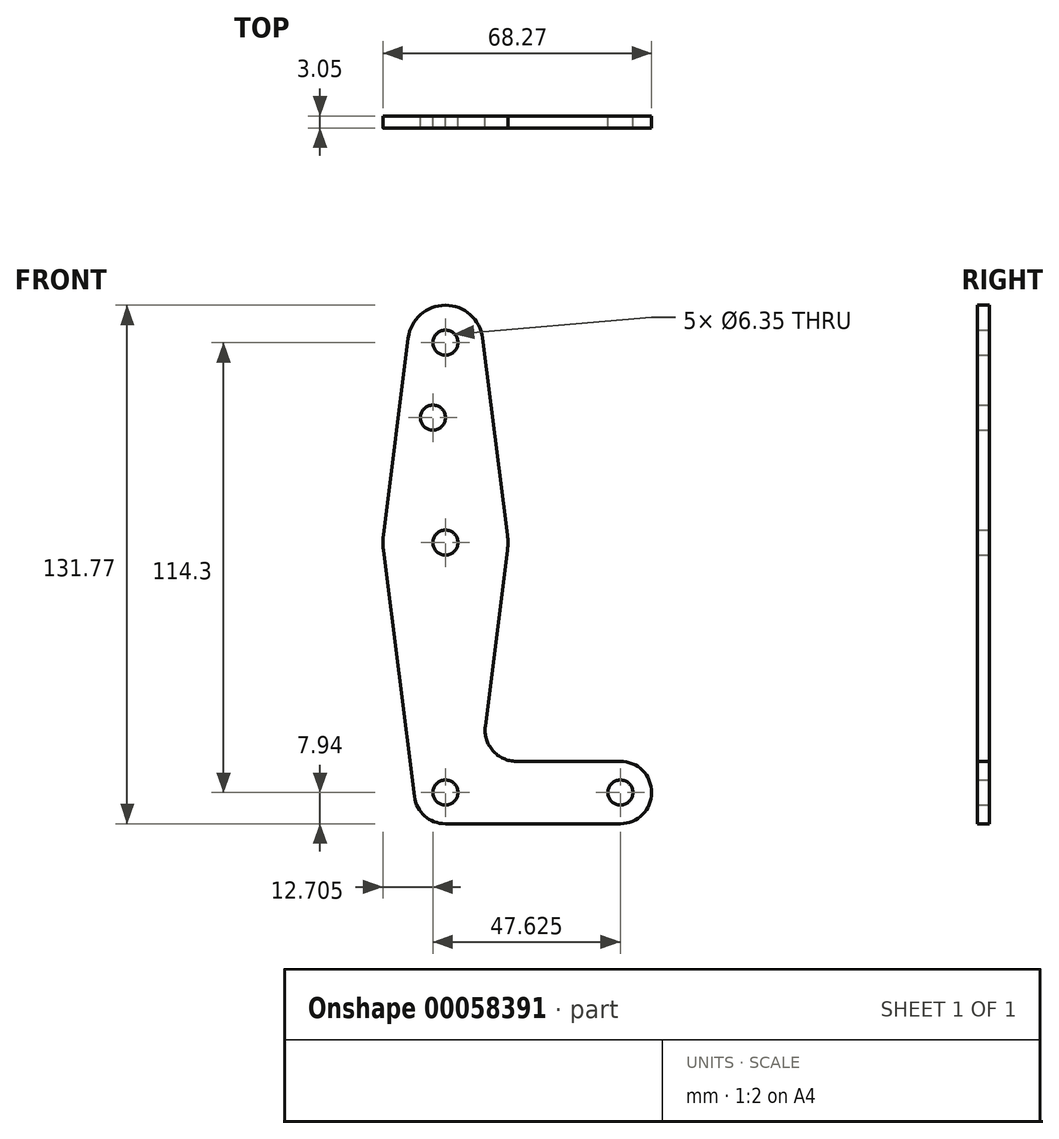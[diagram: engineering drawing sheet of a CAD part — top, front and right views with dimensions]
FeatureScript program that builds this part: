
annotation { "Feature Type Name" : "Feature", "Feature Type Description" : "" }
export const myFeature = defineFeature(function(context is Context, id is Id, definition is map)
    precondition{}
    {
        {
            var Q0;
            Q0=qCreatedBy(makeId("Front.planeOp"),FACE);
            var sketch = newSketch(context, id + "F0", { "sketchPlane" : qUnion([Q0])});
            skCircle(sketch, "E0", {"center": v(0, 0) * mm, "radius": 7.94 * mm});
            skCircle(sketch, "E1", {"center": v(0, 63.5) * mm, "radius": 15.88 * mm});
            skCircle(sketch, "E2", {"center": v(0, 114.3) * mm, "radius": 9.53 * mm});
            skCircle(sketch, "E3", {"center": v(44.45, 0) * mm, "radius": 7.94 * mm});
            skLineSegment(sketch, "E4", {"start": v(-9.45, 115.5) * mm, "end": v(-15.75, 65.48) * mm});
            skLineSegment(sketch, "E5", {"start": v(9.45, 115.5) * mm, "end": v(15.75, 65.48) * mm});
            skLineSegment(sketch, "E6", {"start": v(-15.75, 61.52) * mm, "end": v(-7.88, -1) * mm});
            skLineSegment(sketch, "E7", {"start": v(15.75, 61.52) * mm, "end": v(10.13, 16.88) * mm});
            skLineSegment(sketch, "E8", {"start": v(18.01, 7.94) * mm, "end": v(44.45, 7.94) * mm});
            skLineSegment(sketch, "E9", {"start": v(0, -7.94) * mm, "end": v(44.45, -7.94) * mm});
            skCircle(sketch, "E10", {"center": v(0, 114.3) * mm, "radius": 3.18 * mm});
            skLineSegment(sketch, "E11", {"start": v(0, 0) * mm, "end": v(0, 144.52) * mm, "construction": true});
            skLineSegment(sketch, "E12", {"start": v(0, 0) * mm, "end": v(105.27, 0) * mm, "construction": true});
            skCircle(sketch, "E13", {"center": v(0, 63.5) * mm, "radius": 3.18 * mm});
            skCircle(sketch, "E14", {"center": v(44.45, 0) * mm, "radius": 3.18 * mm});
            skCircle(sketch, "E15", {"center": v(0, 0) * mm, "radius": 3.18 * mm});
            skPoint(sketch, "E16.newPointA", {"position": v(0, 7.94) * mm});
            skArc(sketch, "E16.filletArc", {"start": v(10.13, 16.88) * mm, "mid": v(12.05, 10.63) * mm, "end": v(18.01, 7.94) * mm});
            skCircle(sketch, "E17", {"center": v(-3.18, 95.25) * mm, "radius": 3.18 * mm});
            skPoint(sketch, "E17.first.point", {"position": v(0, 95.25) * mm});
            skPoint(sketch, "E17.second.point", {"position": v(-5.92, 96.84) * mm});
            skPoint(sketch, "E17.third.point", {"position": v(-5.67, 93.29) * mm});
            skSolve(sketch);
        }
        {
            var Q0;
            Q0=makeQuery(id+"F0.imprint","IMPRINT",FACE,{"disambiguationData":[TD([[makeQuery(id+"F0.imprint","IMPRINT",EDGE,{"derivedFrom":sQuery(id+"F0.wireOp",EDGE,"E10")}),-1.0]])]});
            var Q1;
            {var subQ1=sQuery(id+"F0.wireOp",EDGE,"E4");Q1=makeQuery(id+"F0.imprint","IMPRINT",FACE,{"disambiguationData":[TD([[makeQuery(id+"F0.imprint","IMPRINT",EDGE,{"derivedFrom":subQ1}),1.0]])]});}
            var Q2;
            Q2=makeQuery(id+"F0.imprint","IMPRINT",FACE,{"disambiguationData":[TD([[makeQuery(id+"F0.imprint","IMPRINT",EDGE,{"derivedFrom":sQuery(id+"F0.wireOp",EDGE,"E13")}),-1.0]])]});
            var Q3;
            {var subQ0=sQuery(id+"F0.wireOp",EDGE,"E6");Q3=makeQuery(id+"F0.imprint","IMPRINT",FACE,{"disambiguationData":[TD([[makeQuery(id+"F0.imprint","IMPRINT",EDGE,{"derivedFrom":subQ0}),1.0]])]});}
            var Q4;
            Q4=makeQuery(id+"F0.imprint","IMPRINT",FACE,{"disambiguationData":[TD([[makeQuery(id+"F0.imprint","IMPRINT",EDGE,{"derivedFrom":sQuery(id+"F0.wireOp",EDGE,"E15")}),-1.0]])]});
            var Q5;
            Q5=makeQuery(id+"F0.imprint","IMPRINT",FACE,{"disambiguationData":[TD([[makeQuery(id+"F0.imprint","IMPRINT",EDGE,{"derivedFrom":sQuery(id+"F0.wireOp",EDGE,"E14")}),-1.0]])]});
            extrude(context, id + "F1", {"entities" : qUnion([Q0, Q1, Q2, Q3, Q4, Q5]), "depth" : 3.05 * mm});
        }
    });
